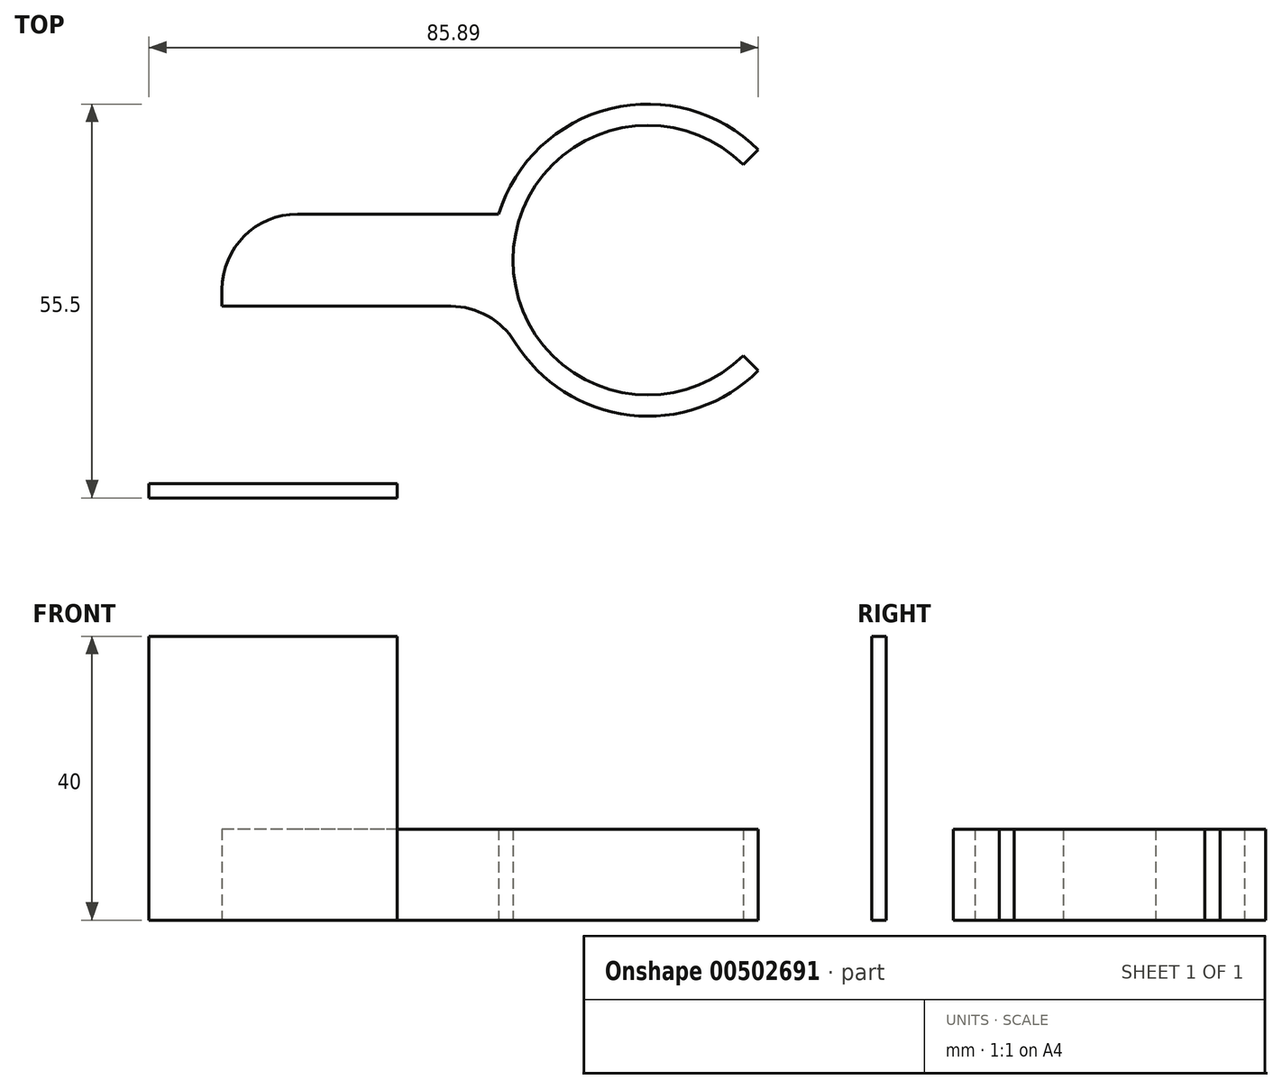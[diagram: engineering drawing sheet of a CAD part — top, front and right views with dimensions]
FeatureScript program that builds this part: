
annotation { "Feature Type Name" : "Feature", "Feature Type Description" : "" }
export const myFeature = defineFeature(function(context is Context, id is Id, definition is map)
    precondition{}
    {
        {
            var Q0;
            Q0=qCreatedBy(makeId("Top.planeOp"),FACE);
            var sketch = newSketch(context, id + "F0", { "sketchPlane" : qUnion([Q0])});
            skCircle(sketch, "E0", {"center": v(0, 0) * mm, "radius": 19 * mm});
            skCircle(sketch, "E1.0", {"center": v(0, 0) * mm, "radius": 22 * mm});
            skLineSegment(sketch, "E2.bottom", {"start": v(0, 6.5) * mm, "end": v(-60, 6.5) * mm});
            skLineSegment(sketch, "E2.top", {"start": v(0, -6.5) * mm, "end": v(-60, -6.5) * mm});
            skLineSegment(sketch, "E2.left", {"start": v(0, 6.5) * mm, "end": v(0, -6.5) * mm});
            skLineSegment(sketch, "E2.right", {"start": v(-60, 6.5) * mm, "end": v(-60, -6.5) * mm});
            skLineSegment(sketch, "E3.bottom", {"start": v(-60, -6.5) * mm, "end": v(-47, -6.5) * mm});
            skLineSegment(sketch, "E3.top", {"start": v(-60, -31.5) * mm, "end": v(-47, -31.5) * mm});
            skLineSegment(sketch, "E3.left", {"start": v(-60, -6.5) * mm, "end": v(-60, -31.5) * mm});
            skLineSegment(sketch, "E3.right", {"start": v(-47, -6.5) * mm, "end": v(-47, -31.5) * mm});
            skLineSegment(sketch, "E4.bottom", {"start": v(-70.33, -33.5) * mm, "end": v(-35.33, -33.5) * mm});
            skLineSegment(sketch, "E4.top", {"start": v(-70.33, -31.5) * mm, "end": v(-35.33, -31.5) * mm});
            skLineSegment(sketch, "E4.left", {"start": v(-70.33, -33.5) * mm, "end": v(-70.33, -31.5) * mm});
            skLineSegment(sketch, "E4.right", {"start": v(-35.33, -33.5) * mm, "end": v(-35.33, -31.5) * mm});
            skLineSegment(sketch, "E5", {"start": v(0, 0) * mm, "end": v(22.4, 22.4) * mm});
            skLineSegment(sketch, "E6", {"start": v(0, 0) * mm, "end": v(22.82, -22.82) * mm});
            skSolve(sketch);
        }
        {
            var Q0;
            {var subQ0=sQuery(id+"F0.wireOp",EDGE,"E2.right");Q0=makeQuery(id+"F0.imprint","IMPRINT",FACE,{"disambiguationData":[TD([[makeQuery(id+"F0.imprint","IMPRINT",EDGE,{"derivedFrom":subQ0}),1.0]])]});}
            var Q1;
            Q1=makeQuery(id+"F0.imprint","IMPRINT",FACE,{"disambiguationData":[TD([[makeQuery(id+"F0.imprint","IMPRINT",EDGE,{"derivedFrom":sQuery(id+"F0.wireOp",EDGE,"E3.bottom")}),-1.0]])]});
            var Q2;
            {var subQ0=sQuery(id+"F0.wireOp",EDGE,"E2.bottom");var subQ1=sQuery(id+"F0.wireOp",EDGE,"E0");var subQ2=makeQuery(id+"F0.imprint","INTERSECT",VERTEX,{"derivedFrom":[subQ1,subQ0]});Q2=makeQuery(id+"F0.imprint","IMPRINT",FACE,{"disambiguationData":[TD([[makeQuery(id+"F0.imprint","IMPRINT",EDGE,{"disambiguationData":[TD([[subQ2,-1.0]])],"derivedFrom":subQ1}),-1.0]])]});}
            var Q3;
            {var subQ0=sQuery(id+"F0.wireOp",EDGE,"E2.top");var subQ1=sQuery(id+"F0.wireOp",EDGE,"E0");var subQ2=makeQuery(id+"F0.imprint","INTERSECT",VERTEX,{"derivedFrom":[subQ1,subQ0]});Q3=makeQuery(id+"F0.imprint","IMPRINT",FACE,{"disambiguationData":[TD([[makeQuery(id+"F0.imprint","IMPRINT",EDGE,{"disambiguationData":[TD([[subQ2,-1.0]])],"derivedFrom":subQ1}),-1.0]])]});}
            var Q4;
            {var subQ0=sQuery(id+"F0.wireOp",EDGE,"E2.bottom");var subQ1=sQuery(id+"F0.wireOp",EDGE,"E0");var subQ2=makeQuery(id+"F0.imprint","INTERSECT",VERTEX,{"derivedFrom":[subQ1,subQ0]});Q4=makeQuery(id+"F0.imprint","IMPRINT",FACE,{"disambiguationData":[TD([[makeQuery(id+"F0.imprint","IMPRINT",EDGE,{"disambiguationData":[TD([[subQ2,1.0]])],"derivedFrom":subQ1}),-1.0]])]});}
            extrude(context, id + "F1", {"entities" : qUnion([Q0, Q1, Q2, Q3, Q4]), "depth" : 12.8 * mm});
        }
        {
            var Q0;
            Q0=makeQuery(id+"F0.imprint","IMPRINT",FACE,{"disambiguationData":[TD([[makeQuery(id+"F0.imprint","IMPRINT",EDGE,{"derivedFrom":sQuery(id+"F0.wireOp",EDGE,"E4.bottom")}),1.0]])]});
            extrude(context, id + "F2", {"entities" : qUnion([Q0]), "operationType" : NewBodyOperationType.ADD, "depth" : 40 * mm});
        }
        {
            var Q0;
            Q0=makeQuery(id+"F1.opExtrude","SWEPT_EDGE",EDGE,{"disambiguationData":[OSD([sQuery(id+"F0.wireOp",EDGE,"E2.bottom"),sQuery(id+"F0.wireOp",EDGE,"E2.right")])]});
            var Q1;
            Q1=makeQuery(id+"F1.opExtrude","SWEPT_EDGE",EDGE,{"disambiguationData":[OSD([sQuery(id+"F0.wireOp",EDGE,"E2.top"),sQuery(id+"F0.wireOp",EDGE,"E3.bottom"),sQuery(id+"F0.wireOp",EDGE,"E3.right")])]});
            fillet(context, id + "F3", {"entities" : qUnion([Q0, Q1]), "radius" : 10.62 * mm, "tangentPropagation" : true, "allowEdgeOverflow" : false});
        }
    });
